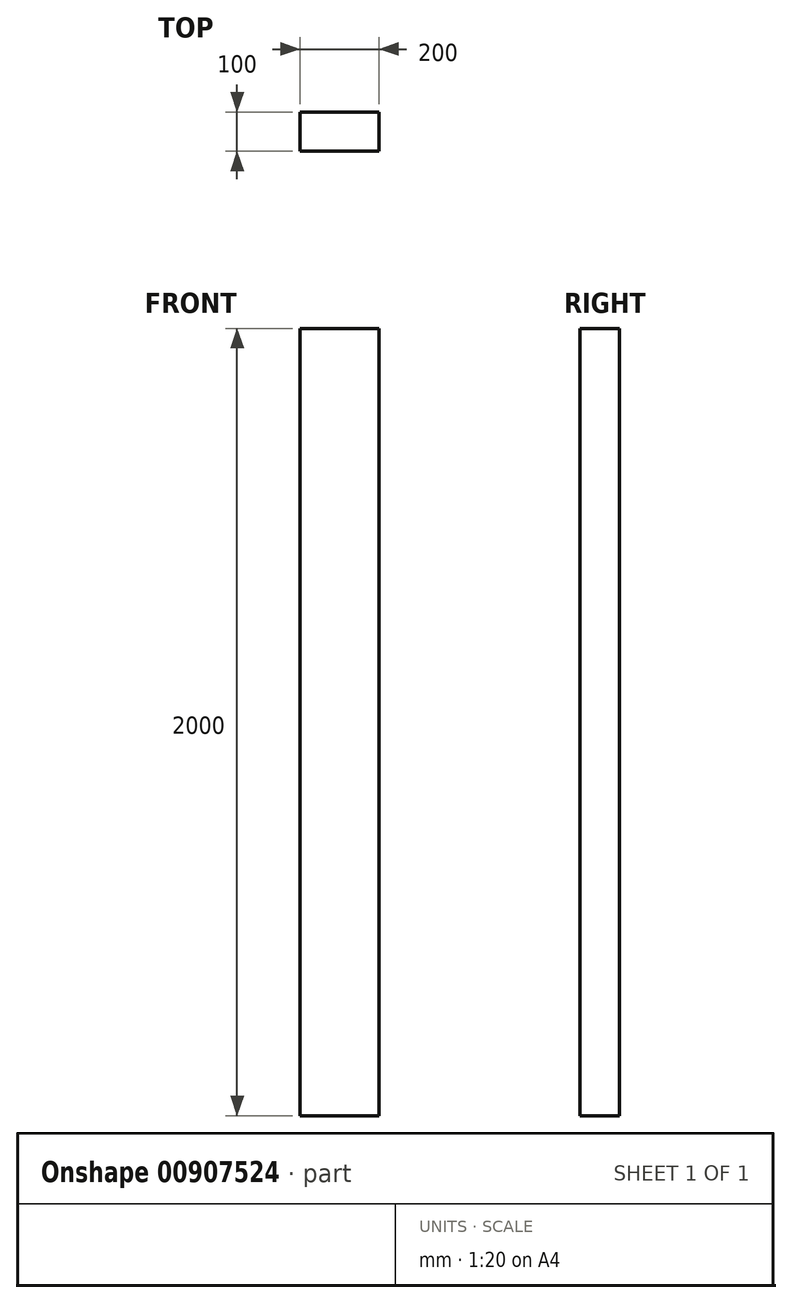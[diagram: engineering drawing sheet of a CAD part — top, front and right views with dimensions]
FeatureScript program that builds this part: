
annotation { "Feature Type Name" : "Feature", "Feature Type Description" : "" }
export const myFeature = defineFeature(function(context is Context, id is Id, definition is map)
    precondition{}
    {
        {
            var Q0;
            Q0=qCreatedBy(makeId("Top.planeOp"),FACE);
            var sketch = newSketch(context, id + "F0", { "sketchPlane" : qUnion([Q0])});
            skLineSegment(sketch, "E0.bottom", {"start": v(100, -50) * mm, "end": v(-100, -50) * mm});
            skLineSegment(sketch, "E0.top", {"start": v(100, 50) * mm, "end": v(-100, 50) * mm});
            skLineSegment(sketch, "E0.left", {"start": v(100, -50) * mm, "end": v(100, 50) * mm});
            skLineSegment(sketch, "E0.right", {"start": v(-100, -50) * mm, "end": v(-100, 50) * mm});
            skPoint(sketch, "E0.middle", {"position": v(0, 0) * mm});
            skSolve(sketch);
        }
        {
            var Q0;
            Q0 = qSketchRegion(id + "F0", true);
            extrude(context, id + "F1", {"entities" : qUnion([Q0]), "depth" : 2000 * mm, "offsetDistance" : 25 * mm});
        }
    });
